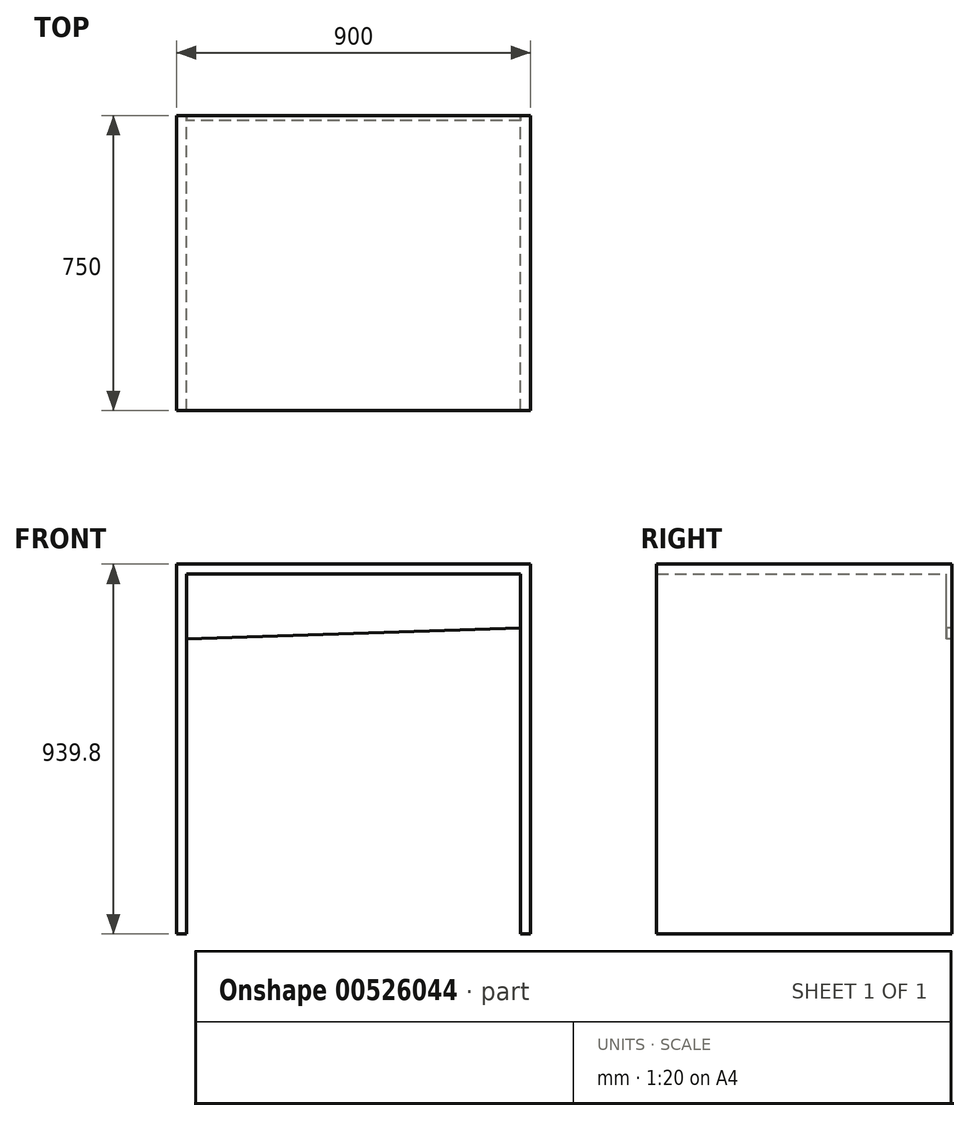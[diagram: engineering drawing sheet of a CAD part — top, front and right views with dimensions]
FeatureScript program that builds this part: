
annotation { "Feature Type Name" : "Feature", "Feature Type Description" : "" }
export const myFeature = defineFeature(function(context is Context, id is Id, definition is map)
    precondition{}
    {
        {
            var Q0;
            Q0=qCreatedBy(makeId("Top.planeOp"),FACE);
            var sketch = newSketch(context, id + "F0", { "sketchPlane" : qUnion([Q0])});
            skLineSegment(sketch, "E0.bottom", {"start": v(450, -375) * mm, "end": v(-450, -375) * mm});
            skLineSegment(sketch, "E0.top", {"start": v(450, 375) * mm, "end": v(-450, 375) * mm});
            skLineSegment(sketch, "E0.left", {"start": v(450, -375) * mm, "end": v(450, 375) * mm});
            skLineSegment(sketch, "E0.right", {"start": v(-450, -375) * mm, "end": v(-450, 375) * mm});
            skPoint(sketch, "E0.middle", {"position": v(0, 0) * mm});
            skSolve(sketch);
        }
        {
            var Q0;
            Q0=qSketchRegion(id+"F0",true);
            extrude(context, id + "F1", {"entities" : qUnion([Q0]), "depth" : 25.4 * mm});
        }
        {
            var Q0;
            Q0=makeQuery(id+"F1.opExtrude","CAP_FACE",FACE,{"disambiguationData":[OSD([sQuery(id+"F0.wireOp",EDGE,"E0.bottom"),sQuery(id+"F0.wireOp",EDGE,"E0.top"),sQuery(id+"F0.wireOp",EDGE,"E0.left"),sQuery(id+"F0.wireOp",EDGE,"E0.right")])],"isStart":true});
            var sketch = newSketch(context, id + "F2", { "sketchPlane" : qUnion([Q0])});
            skLineSegment(sketch, "E1", {"start": v(-450, 375) * mm, "end": v(-424.6, 375) * mm});
            skLineSegment(sketch, "E2", {"start": v(-424.6, 375) * mm, "end": v(-424.6, -361.6) * mm});
            skLineSegment(sketch, "E3", {"start": v(-424.6, -361.6) * mm, "end": v(-450, -375) * mm});
            skLineSegment(sketch, "E4", {"start": v(-450, -375) * mm, "end": v(-450, 375) * mm});
            skLineSegment(sketch, "E5", {"start": v(450, 375) * mm, "end": v(424.6, 375) * mm});
            skLineSegment(sketch, "E6", {"start": v(424.6, 375) * mm, "end": v(424.6, -361.6) * mm});
            skLineSegment(sketch, "E7", {"start": v(424.6, -361.6) * mm, "end": v(450, -375) * mm});
            skLineSegment(sketch, "E8", {"start": v(450, -375) * mm, "end": v(450, 375) * mm});
            skLineSegment(sketch, "E9", {"start": v(-450, -375) * mm, "end": v(450, -375) * mm});
            skLineSegment(sketch, "E10", {"start": v(424.6, -361.6) * mm, "end": v(-424.6, -361.6) * mm});
            skSolve(sketch);
        }
        {
            var Q0;
            Q0=qSketchRegion(id+"F2",true);
            extrude(context, id + "F3", {"entities" : qUnion([Q0]), "operationType" : NewBodyOperationType.ADD, "depth" : 914.4 * mm});
        }
        {
            var Q0;
            Q0=makeQuery(id+"F3.opExtrude","SWEPT_FACE",FACE,{"disambiguationData":[OSD([sQuery(id+"F2.wireOp",EDGE,"E10")])]});
            var sketch = newSketch(context, id + "F4", { "sketchPlane" : qUnion([Q0])});
            skLineSegment(sketch, "E11", {"start": v(-424.6, -164.4) * mm, "end": v(-424.6, -914.4) * mm});
            skLineSegment(sketch, "E12", {"start": v(-424.6, -914.4) * mm, "end": v(424.6, -914.4) * mm});
            skLineSegment(sketch, "E13", {"start": v(424.6, -914.4) * mm, "end": v(424.6, -137.32) * mm});
            skLineSegment(sketch, "E14", {"start": v(424.6, -137.32) * mm, "end": v(-424.6, -164.4) * mm});
            skSolve(sketch);
        }
        {
            var Q0;
            Q0=qSketchRegion(id+"F4",true);
            extrude(context, id + "F5", {"entities" : qUnion([Q0]), "operationType" : NewBodyOperationType.REMOVE, "oppositeDirection" : true, "depth" : 25.4 * mm});
        }
    });
